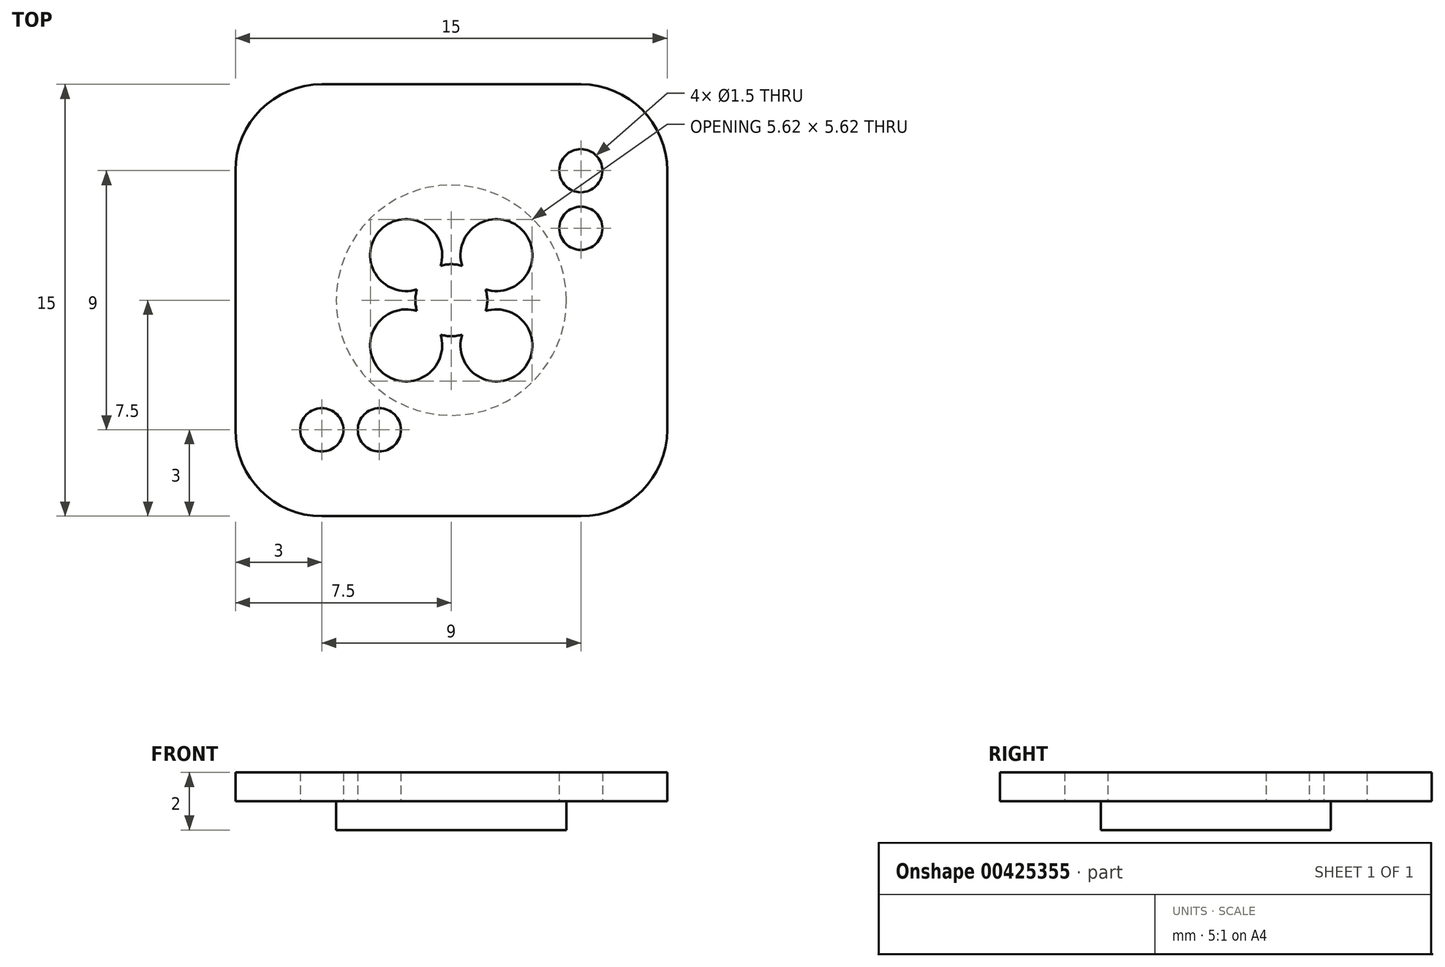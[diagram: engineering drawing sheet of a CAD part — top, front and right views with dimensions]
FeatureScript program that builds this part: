
annotation { "Feature Type Name" : "Feature", "Feature Type Description" : "" }
export const myFeature = defineFeature(function(context is Context, id is Id, definition is map)
    precondition{}
    {
        {
            var Q0;
            Q0=qCreatedBy(makeId("Top.planeOp"),FACE);
            var sketch = newSketch(context, id + "F0", { "sketchPlane" : qUnion([Q0])});
            skCircle(sketch, "E0", {"center": v(0, 0) * mm, "radius": 1.25 * mm});
            skCircle(sketch, "E1", {"center": v(0, 0) * mm, "radius": 4 * mm});
            skCircle(sketch, "E2", {"center": v(-1.57, 1.57) * mm, "radius": 1.25 * mm});
            skCircle(sketch, "E3", {"center": v(1.57, 1.57) * mm, "radius": 1.25 * mm});
            skCircle(sketch, "E4", {"center": v(-1.57, -1.57) * mm, "radius": 1.25 * mm});
            skCircle(sketch, "E5", {"center": v(1.57, -1.57) * mm, "radius": 1.25 * mm});
            skSolve(sketch);
        }
        {
            var Q0;
            Q0=makeQuery(id+"F0.imprint","IMPRINT",FACE,{"disambiguationData":[TD([[makeQuery(id+"F0.imprint","IMPRINT",EDGE,{"derivedFrom":sQuery(id+"F0.wireOp",EDGE,"E1")}),1.0]])]});
            extrude(context, id + "F1", {"entities" : qUnion([Q0]), "oppositeDirection" : true, "depth" : 1 * mm});
        }
        {
            var Q0;
            Q0=makeQuery(id+"F1.opExtrude","CAP_FACE",FACE,{"disambiguationData":[OSD([sQuery(id+"F0.wireOp",EDGE,"E0"),sQuery(id+"F0.wireOp",EDGE,"E1")])],"isStart":true});
            var sketch = newSketch(context, id + "F2", { "sketchPlane" : qUnion([Q0])});
            skCircle(sketch, "E6", {"center": v(0, 0) * mm, "radius": 1.25 * mm});
            skCircle(sketch, "E7", {"center": v(0, 0) * mm, "radius": 5 * mm});
            skLineSegment(sketch, "E8.bottom", {"start": v(-7.5, -7.5) * mm, "end": v(7.5, -7.5) * mm});
            skLineSegment(sketch, "E8.top", {"start": v(-7.5, 7.5) * mm, "end": v(7.5, 7.5) * mm});
            skLineSegment(sketch, "E8.left", {"start": v(-7.5, -7.5) * mm, "end": v(-7.5, 7.5) * mm});
            skLineSegment(sketch, "E8.right", {"start": v(7.5, -7.5) * mm, "end": v(7.5, 7.5) * mm});
            skSolve(sketch);
        }
        {
            var Q0;
            Q0=makeQuery(id+"F2.imprint","IMPRINT",FACE,{"disambiguationData":[TD([[makeQuery(id+"F2.imprint","IMPRINT",EDGE,{"derivedFrom":sQuery(id+"F2.wireOp",EDGE,"E7")}),-1.0]])]});
            var Q1;
            Q1=makeQuery(id+"F2.imprint","IMPRINT",FACE,{"disambiguationData":[TD([[makeQuery(id+"F2.imprint","IMPRINT",EDGE,{"derivedFrom":sQuery(id+"F2.wireOp",EDGE,"E7")}),1.0]])]});
            var Q2;
            Q2=makeQuery(id+"F2.imprint","IMPRINT",FACE,{"disambiguationData":[TD([[makeQuery(id+"F2.imprint","IMPRINT",EDGE,{"derivedFrom":makeQuery(id+"F1.opExtrude","CAP_EDGE",EDGE,{"disambiguationData":[OSD([sQuery(id+"F0.wireOp",EDGE,"E1")])],"isStart":true})}),1.0]])]});
            extrude(context, id + "F3", {"entities" : qUnion([Q0, Q1, Q2]), "operationType" : NewBodyOperationType.ADD, "depth" : 1 * mm});
        }
        {
            var Q0;
            Q0=makeQuery(id+"F3.opExtrude","SWEPT_EDGE",EDGE,{"disambiguationData":[OSD([sQuery(id+"F2.wireOp",EDGE,"E8.bottom"),sQuery(id+"F2.wireOp",EDGE,"E8.left")])]});
            var Q1;
            Q1=makeQuery(id+"F3.opExtrude","SWEPT_EDGE",EDGE,{"disambiguationData":[OSD([sQuery(id+"F2.wireOp",EDGE,"E8.bottom"),sQuery(id+"F2.wireOp",EDGE,"E8.right")])]});
            var Q2;
            Q2=makeQuery(id+"F3.opExtrude","SWEPT_EDGE",EDGE,{"disambiguationData":[OSD([sQuery(id+"F2.wireOp",EDGE,"E8.top"),sQuery(id+"F2.wireOp",EDGE,"E8.left")])]});
            var Q3;
            Q3=makeQuery(id+"F3.opExtrude","SWEPT_EDGE",EDGE,{"disambiguationData":[OSD([sQuery(id+"F2.wireOp",EDGE,"E8.top"),sQuery(id+"F2.wireOp",EDGE,"E8.right")])]});
            fillet(context, id + "F4", {"entities" : qUnion([Q0, Q1, Q2, Q3]), "radius" : 3 * mm, "tangentPropagation" : true, "allowEdgeOverflow" : false});
        }
        {
            var Q0;
            Q0=makeQuery(id+"F3.opExtrude","CAP_FACE",FACE,{"disambiguationData":[OSD([sQuery(id+"F2.wireOp",EDGE,"E6"),sQuery(id+"F2.wireOp",EDGE,"E8.bottom"),sQuery(id+"F2.wireOp",EDGE,"E8.top"),sQuery(id+"F2.wireOp",EDGE,"E8.left"),sQuery(id+"F2.wireOp",EDGE,"E8.right")])],"isStart":true});
            var sketch = newSketch(context, id + "F5", { "sketchPlane" : qUnion([Q0])});
            skCircle(sketch, "E9", {"center": v(-4.5, 4.5) * mm, "radius": 0.75 * mm});
            skCircle(sketch, "E10", {"center": v(-2.5, 4.5) * mm, "radius": 0.75 * mm});
            skCircle(sketch, "E11", {"center": v(4.5, -4.5) * mm, "radius": 0.75 * mm});
            skCircle(sketch, "E12", {"center": v(4.5, -2.5) * mm, "radius": 0.75 * mm});
            skSolve(sketch);
        }
        {
            var Q0;
            Q0=qSketchRegion(id+"F5",true);
            extrude(context, id + "F6", {"entities" : qUnion([Q0]), "operationType" : NewBodyOperationType.REMOVE, "oppositeDirection" : true, "depth" : 25 * mm});
        }
    });
